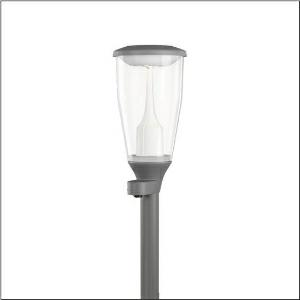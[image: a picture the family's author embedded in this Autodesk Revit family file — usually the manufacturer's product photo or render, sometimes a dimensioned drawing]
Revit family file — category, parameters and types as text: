
# Revit family: dl_11_iq___st1_2a_5xa5565eu14hp00022_7835
name_source: partatom
category: Lighting Fixtures
units: mm (PartAtom-declared; Revit-internal decimal feet)

## family parameters
Cut with Voids When Loaded = No
Host = Face
Light Source = No
Part Type = Normal
Room Calculation Point = No
Round Connector Dimension = Use Diameter
Shared = No

## types (1)
- --- (1 x LED, 4790 lm, 33.5 W, 3000K)
    Apparent Load = 34 VA
    CIE Flux Codes = 23 60 93 95 100
    Color Rendering = 70
    Color Temperature = 3000K
    Default Elevation = 1800 mm
    Description = DL 11 iQ, mast luminaire, Module 540 iQ-SR, primary light control with 3 zone facetted reflector, of plastic, silver coated, highly specular, structured, primary optical cover: cover, of PMMA, transparent, light distribution: ST1.2a, light emission: direct distribution, primary light characteristic: asymmetric, installation type: post-top, LED, High Power LED, rated luminous flux: 4.790lm, luminous efficacy: 143lm/W, light colour: 730, colour temperature: 3000K, control gear: iQ-Street Remote, D4i with power reduction, control: pre-setting: logarithmic dimming characteristic, Street-Remote, Auto-Match, Temp-Guard, Lumen-Switch, Night-Set, Smart-Wire, Light-Fading, Desk-Remote (wireless, voltage-free reading and setting of iQ features in the workshop via application-optimized NFC function/RFID function), optimised constant luminous flux control (CLO 2.0), mains connection: 220..240V, AC, 50/60Hz, connection cable pre-assembled, cable length: 5,5m, start of lifetime: 34W, end of service life: 36W, reduction: 15W, luminaire housing, upper part, of diecast aluminium, coated, Siteco® metallic grey (DB 702S), spigot size: 60mm (post-top), mounting height: 3..5m, post-top mast mounting element, of diecast aluminium, coated, Siteco® metallic grey (DB 702S), Module 540 iQ-SR, traffic white (RAL 9016), equipment: Power, Smart Interface below, protection rating (complete): IP66, insulation class (complete): insulation class II (safety insulation), certification: CE, ENEC, ENEC+, VDE, impact resistance: IK07, packaging unit: 1 piece

Light Distribution: ST1.2a
    Height = 665 mm
    Lamp = 1 x LED
    Lamp Light Flux = 4790 lm
    Lamp Power = 33.5 W
    Lamp count = 1
    Length = 334 mm
    Luminous efficacy = 143 lm/W
    Manufacturer = Siteco
    ModVariant = No
    Model = 5XA5565EU14HP00022
    Number of Poles = 1
    OnlyDefault = Yes
    Power Factor = 1
    Product Name = DL 11 iQ | ST1.2a
    Product group = mast luminaire | pylon top
    ProductGroupID = 6100
    Protection Class = Protection class II
    Protection Degree = IP 66
    RLX_Detail_Level = 1
    RLX_Emergency_Light_Flux = 0 lm
    RLX_Emergency_Type = 0
    RLX_Emergency_Type_DB = No
    RlxData = <blob elided: 160585 chars, md5=ba654acb>
    Socket = socket
    Standby Power = 0 W
    System Light Flux = 4790 lm
    System Power = 34 W
    Type Comments = factory setting: luminous flux: 100 % | dim-lin: 254 | 695 mA
    Type Image = l_1337539.jpg
    URL = http://relux.com
    VarID = @adj_034044
    Voltage = 0 V
    Weight = 0.00 kg
    Width = 0 mm  [stored 0 ft]

note: [stored X ft] marks values corroborated as IEEE doubles in the binary element streams (Revit-internal decimal feet)

## geometry (parser evidence)
native form markers: Blend x4, Sweep x12
no freeform markers — native parametric forms only
